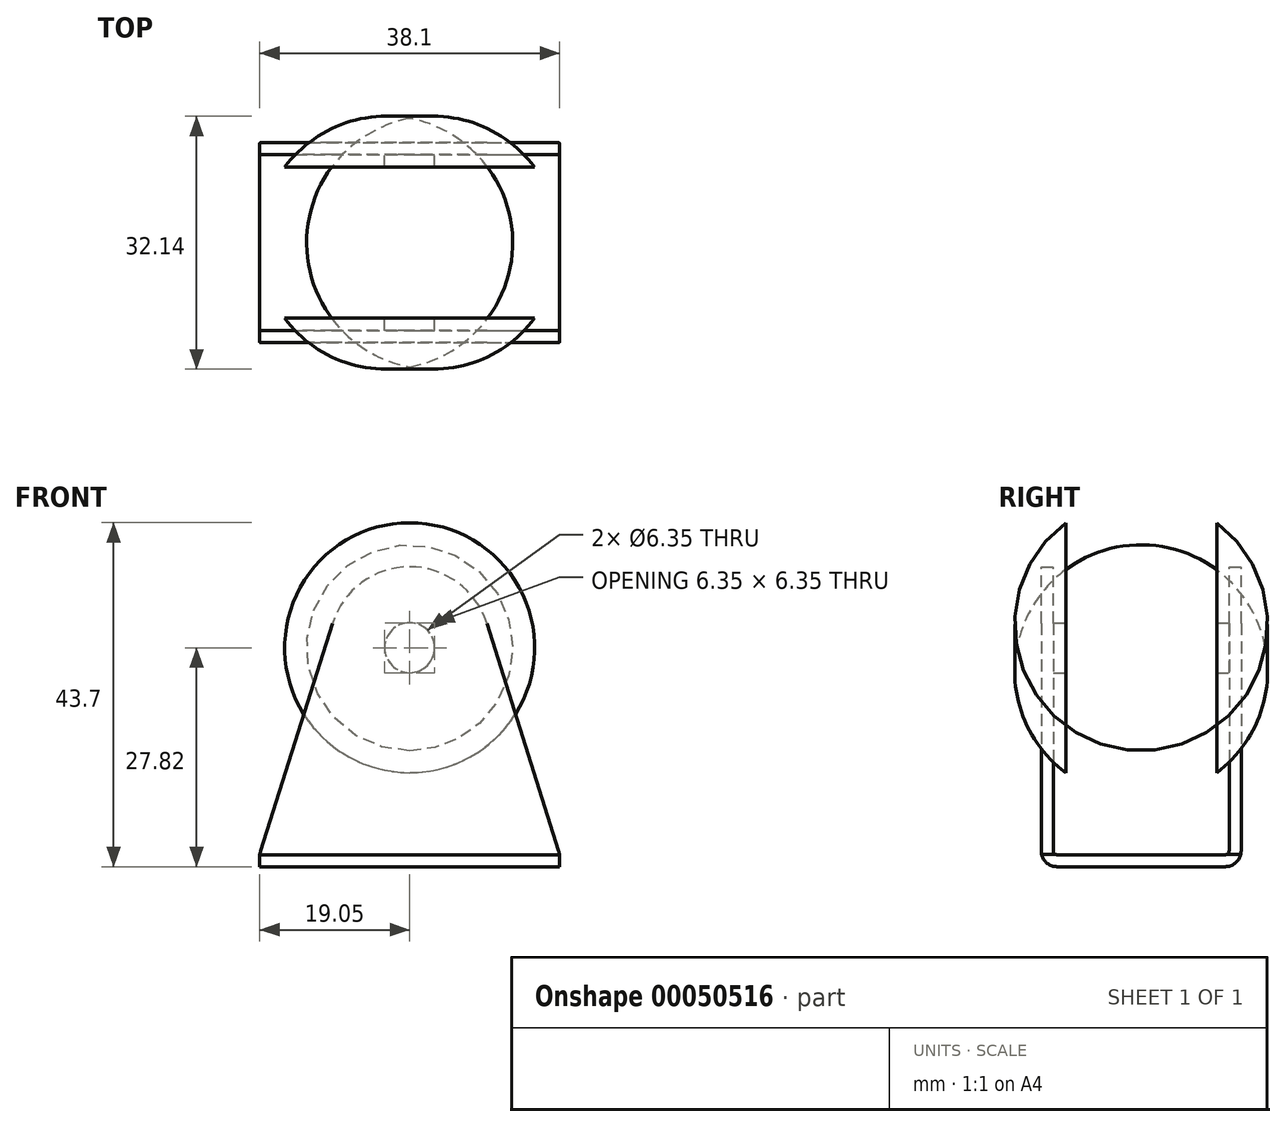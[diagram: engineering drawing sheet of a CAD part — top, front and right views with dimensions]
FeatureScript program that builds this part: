
annotation { "Feature Type Name" : "Feature", "Feature Type Description" : "" }
export const myFeature = defineFeature(function(context is Context, id is Id, definition is map)
    precondition{}
    {
        {
            var Q0;
            Q0=qCreatedBy(makeId("Front.planeOp"),FACE);
            var sketch = newSketch(context, id + "F0", { "sketchPlane" : qUnion([Q0])});
            skArc(sketch, "E0", {"start": v(9.8, 3.1) * mm, "mid": v(0, 10.28) * mm, "end": v(-9.8, 3.1) * mm});
            skLineSegment(sketch, "E1", {"start": v(-9.8, 3.1) * mm, "end": v(-19.05, -26.23) * mm});
            skLineSegment(sketch, "E2", {"start": v(-19.05, -27.82) * mm, "end": v(19.05, -27.82) * mm});
            skLineSegment(sketch, "E3", {"start": v(0, 0) * mm, "end": v(0, -27.82) * mm, "construction": true});
            skLineSegment(sketch, "E4", {"start": v(0, 0) * mm, "end": v(0, 10.28) * mm, "construction": true});
            skLineSegment(sketch, "E5", {"start": v(-19.05, -26.23) * mm, "end": v(-19.05, -27.82) * mm});
            skLineSegment(sketch, "E6", {"start": v(19.05, -27.82) * mm, "end": v(19.05, -26.23) * mm});
            skPoint(sketch, "E7.orphan", {"position": v(-19.55, -27.82) * mm});
            skPoint(sketch, "E8.orphan", {"position": v(19.55, -27.82) * mm});
            skLineSegment(sketch, "E9", {"start": v(9.8, 3.1) * mm, "end": v(19.05, -26.23) * mm});
            skCircle(sketch, "E10", {"center": v(0, 0) * mm, "radius": 6.35 * mm, "construction": true});
            skSolve(sketch);
        }
        {
            var Q0;
            Q0 = qSketchRegion(id + "F0", true);
            extrude(context, id + "F1", {"entities" : qUnion([Q0]), "endBound" : BoundingType.SYMMETRIC, "depth" : 25.4 * mm});
        }
        {
            var Q0;
            Q0=makeQuery(id+"F1.opExtrude","CAP_EDGE",EDGE,{"disambiguationData":[OSD([sQuery(id+"F0.wireOp",EDGE,"E2")])],"isStart":false});
            var Q1;
            Q1=makeQuery(id+"F1.opExtrude","CAP_EDGE",EDGE,{"disambiguationData":[OSD([sQuery(id+"F0.wireOp",EDGE,"E2")])],"isStart":true});
            fillet(context, id + "F2", {"entities" : qUnion([Q0, Q1]), "radius" : 2.03 * mm, "tangentPropagation" : true, "allowEdgeOverflow" : false});
        }
        {
            var Q0;
            Q0=makeQuery(id+"F1.opExtrude","SWEPT_FACE",FACE,{"disambiguationData":[OSD([sQuery(id+"F0.wireOp",EDGE,"E6")])]});
            var Q1;
            Q1=makeQuery(id+"F1.opExtrude","SWEPT_FACE",FACE,{"disambiguationData":[OSD([sQuery(id+"F0.wireOp",EDGE,"E9")])]});
            var Q2;
            Q2=makeQuery(id+"F1.opExtrude","SWEPT_FACE",FACE,{"disambiguationData":[OSD([sQuery(id+"F0.wireOp",EDGE,"E0")])]});
            var Q3;
            Q3=makeQuery(id+"F1.opExtrude","SWEPT_FACE",FACE,{"disambiguationData":[OSD([sQuery(id+"F0.wireOp",EDGE,"E1")])]});
            var Q4;
            Q4=makeQuery(id+"F1.opExtrude","SWEPT_FACE",FACE,{"disambiguationData":[OSD([sQuery(id+"F0.wireOp",EDGE,"E5")])]});
            shell(context, id + "F3", {"entities" : qUnion([Q0, Q1, Q2, Q3, Q4]), "thickness" : 1.52 * mm});
        }
        {
            var Q0;
            Q0=makeQuery(id+"F1.opExtrude","CAP_FACE",FACE,{"disambiguationData":[OSD([sQuery(id+"F0.wireOp",EDGE,"E0"),sQuery(id+"F0.wireOp",EDGE,"E1"),sQuery(id+"F0.wireOp",EDGE,"E2"),sQuery(id+"F0.wireOp",EDGE,"E5"),sQuery(id+"F0.wireOp",EDGE,"E6"),sQuery(id+"F0.wireOp",EDGE,"E9")])],"isStart":true});
            var sketch = newSketch(context, id + "F4", { "sketchPlane" : qUnion([Q0])});
            skCircle(sketch, "E11", {"center": v(0, 0) * mm, "radius": 3.18 * mm});
            skSolve(sketch);
        }
        {
            var Q0;
            Q0 = qSketchRegion(id + "F4", true);
            var Q1;
            Q1=makeQuery(id+"F1.opExtrude","CAP_FACE",FACE,{"disambiguationData":[OSD([sQuery(id+"F0.wireOp",EDGE,"E0"),sQuery(id+"F0.wireOp",EDGE,"E1"),sQuery(id+"F0.wireOp",EDGE,"E2"),sQuery(id+"F0.wireOp",EDGE,"E5"),sQuery(id+"F0.wireOp",EDGE,"E6"),sQuery(id+"F0.wireOp",EDGE,"E9")])],"isStart":false});
            extrude(context, id + "F5", {"entities" : qUnion([Q0]), "operationType" : NewBodyOperationType.ADD, "endBound" : BoundingType.UP_TO_SURFACE, "oppositeDirection" : true, "endBoundEntityFace" : qUnion([Q1]), "depth" : 25.4 * mm});
        }
        {
            var Q0;
            Q0=qCreatedBy(makeId("Right.planeOp"),FACE);
            var sketch = newSketch(context, id + "F6", { "sketchPlane" : qUnion([Q0])});
            skLineSegment(sketch, "E12", {"start": v(-9.59, 0) * mm, "end": v(-9.59, 15.88) * mm});
            skLineSegment(sketch, "E13", {"start": v(-9.59, 0) * mm, "end": v(9.59, 0) * mm});
            skLineSegment(sketch, "E14", {"start": v(9.59, 0) * mm, "end": v(9.59, 15.88) * mm});
            skArc(sketch, "E15", {"start": v(9.59, 15.88) * mm, "mid": v(0, 19.05) * mm, "end": v(-9.59, 15.87) * mm});
            skLineSegment(sketch, "E16", {"start": v(0, 19.05) * mm, "end": v(0, 0) * mm, "construction": true});
            skLineSegment(sketch, "E17", {"start": v(-9.59, 0) * mm, "end": v(-32.64, 0) * mm, "construction": true});
            skSolve(sketch);
        }
        {
            var Q0;
            Q0 = qSketchRegion(id + "F6", true);
            var Q1;
            Q1=sQuery(id+"F6.wireOp",EDGE,"E17");
            revolve(context, id + "F7", {"operationType" : NewBodyOperationType.ADD, "entities" : qUnion([Q0]), "axis" : qUnion([Q1]), "revolveType" : RevolveType.FULL});
        }
    });
